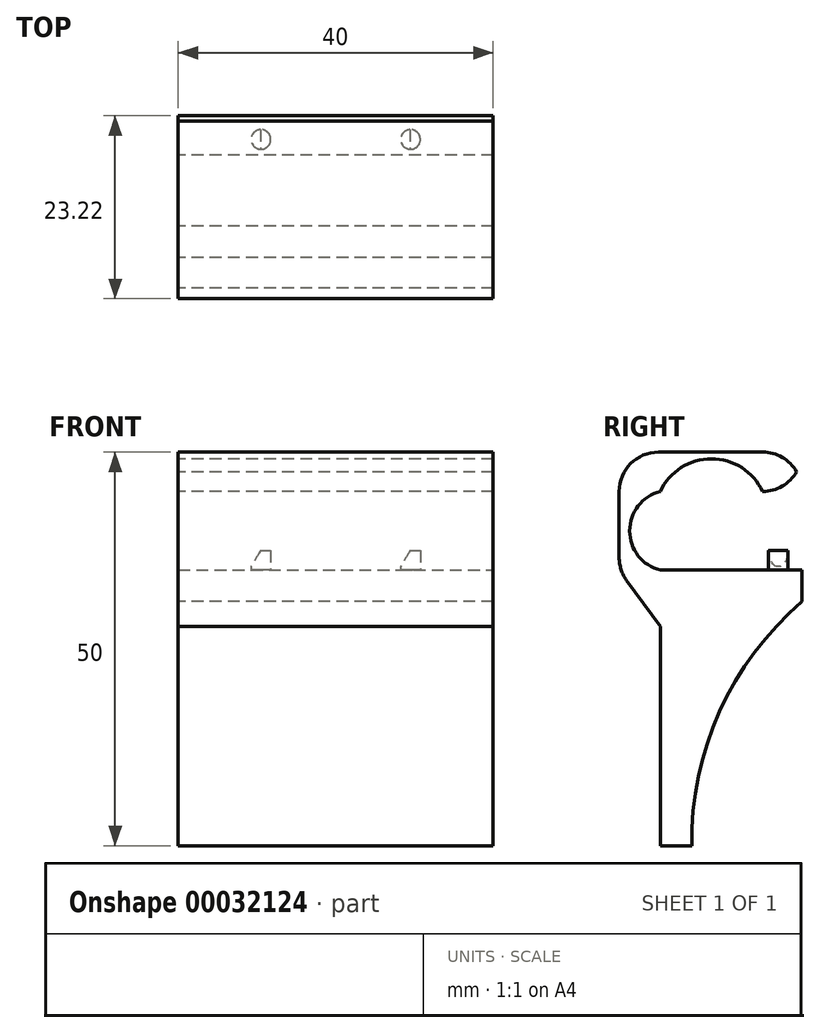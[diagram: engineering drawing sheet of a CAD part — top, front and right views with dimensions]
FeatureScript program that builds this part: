
annotation { "Feature Type Name" : "Feature", "Feature Type Description" : "" }
export const myFeature = defineFeature(function(context is Context, id is Id, definition is map)
    precondition{}
    {
        {
            var Q0;
            Q0=qCreatedBy(makeId("Top.planeOp"),FACE);
            var sketch = newSketch(context, id + "F0", { "sketchPlane" : qUnion([Q0])});
            skLineSegment(sketch, "E0", {"start": v(-9.5, 0) * mm, "end": v(9.5, 0) * mm, "construction": true});
            skCircle(sketch, "E1", {"center": v(-9.5, 0) * mm, "radius": 1.25 * mm});
            skCircle(sketch, "E2.MirrorC", {"center": v(9.5, 0) * mm, "radius": 1.25 * mm});
            skSolve(sketch);
        }
        {
            var Q0;
            Q0=qSketchRegion(id+"F0",true);
            extrude(context, id + "F1", {"entities" : qUnion([Q0]), "depth" : 2.5 * mm});
        }
        {
            var Q0;
            Q0=qCreatedBy(makeId("Top.planeOp"),FACE);
            var sketch = newSketch(context, id + "F2", { "sketchPlane" : qUnion([Q0])});
            skLineSegment(sketch, "E3", {"start": v(0, 0) * mm, "end": v(0, 3) * mm, "construction": true});
            skLineSegment(sketch, "E4", {"start": v(-20, 3) * mm, "end": v(20, 3) * mm});
            skLineSegment(sketch, "E5", {"start": v(-20, 3) * mm, "end": v(-20, -15) * mm});
            skLineSegment(sketch, "E6", {"start": v(20, 3) * mm, "end": v(20, -15) * mm});
            skLineSegment(sketch, "E7", {"start": v(20, -15) * mm, "end": v(-20, -15) * mm});
            skSolve(sketch);
        }
        {
            var Q0;
            Q0=qSketchRegion(id+"F2",true);
            extrude(context, id + "F3", {"entities" : qUnion([Q0]), "operationType" : NewBodyOperationType.ADD, "oppositeDirection" : true, "depth" : 35 * mm});
        }
        {
            var Q0;
            Q0=makeQuery(id+"F3.opExtrude","SWEPT_FACE",FACE,{"disambiguationData":[OSD([sQuery(id+"F2.wireOp",EDGE,"E5")])]});
            var sketch = newSketch(context, id + "F4", { "sketchPlane" : qUnion([Q0])});
            skLineSegment(sketch, "E8", {"start": v(-3, 0) * mm, "end": v(-3, -4) * mm, "construction": true});
            skLineSegment(sketch, "E9", {"start": v(15, -35) * mm, "end": v(11, -35) * mm, "construction": true});
            skArc(sketch, "E10", {"start": v(11, -35) * mm, "mid": v(7.46, -17.94) * mm, "end": v(-3, -4) * mm});
            skLineSegment(sketch, "E11", {"start": v(-3, -4) * mm, "end": v(-3, -35) * mm});
            skLineSegment(sketch, "E12", {"start": v(-3, -35) * mm, "end": v(11, -35) * mm});
            skSolve(sketch);
        }
        {
            var Q0;
            Q0=qSketchRegion(id+"F4",true);
            extrude(context, id + "F5", {"entities" : qUnion([Q0]), "operationType" : NewBodyOperationType.REMOVE, "endBound" : BoundingType.THROUGH_ALL, "oppositeDirection" : true, "depth" : 25 * mm});
        }
        {
            var Q0;
            Q0=makeQuery(id+"F3.opExtrude","SWEPT_FACE",FACE,{"disambiguationData":[OSD([sQuery(id+"F2.wireOp",EDGE,"E5")])]});
            var sketch = newSketch(context, id + "F6", { "sketchPlane" : qUnion([Q0])});
            skLineSegment(sketch, "E13", {"start": v(15, 0) * mm, "end": v(15, 10) * mm, "construction": true});
            skLineSegment(sketch, "E14", {"start": v(15, 10) * mm, "end": v(2, 10) * mm, "construction": true});
            skLineSegment(sketch, "E15", {"start": v(2, 10) * mm, "end": v(-3, 10) * mm});
            skLineSegment(sketch, "E16", {"start": v(-3, 10) * mm, "end": v(-3, 15) * mm});
            skLineSegment(sketch, "E17", {"start": v(-3, 0) * mm, "end": v(-3, 10) * mm, "construction": true});
            skLineSegment(sketch, "E18", {"start": v(15, -7.18) * mm, "end": v(20.22, 0) * mm});
            skLineSegment(sketch, "E19", {"start": v(20.22, 0) * mm, "end": v(20.22, 15) * mm});
            skLineSegment(sketch, "E20", {"start": v(-3, 15) * mm, "end": v(20.22, 15) * mm});
            skLineSegment(sketch, "E21", {"start": v(15, -7.18) * mm, "end": v(15, 0) * mm});
            skArc(sketch, "E22", {"start": v(15, 10) * mm, "mid": v(8.5, 14.13) * mm, "end": v(2, 10) * mm});
            skArc(sketch, "E23", {"start": v(15, 0) * mm, "mid": v(18.88, 5) * mm, "end": v(15, 10) * mm});
            skSolve(sketch);
        }
        {
            var Q0;
            Q0=qSketchRegion(id+"F6",true);
            extrude(context, id + "F7", {"entities" : qUnion([Q0]), "operationType" : NewBodyOperationType.ADD, "oppositeDirection" : true, "depth" : 40 * mm});
        }
        {
            var Q0;
            Q0=makeQuery(id+"F3.opExtrude","SWEPT_FACE",FACE,{"disambiguationData":[OSD([sQuery(id+"F2.wireOp",EDGE,"E4")])]});
            var sketch = newSketch(context, id + "F8", { "sketchPlane" : qUnion([Q0])});
            skLineSegment(sketch, "E24", {"start": v(0, 0) * mm, "end": v(11, 0) * mm, "construction": true});
            skLineSegment(sketch, "E25", {"start": v(11, 0) * mm, "end": v(9.11, 3.27) * mm});
            skLineSegment(sketch, "E26", {"start": v(9.11, 3.27) * mm, "end": v(11, 3.27) * mm});
            skLineSegment(sketch, "E27", {"start": v(11, 3.27) * mm, "end": v(11, 0) * mm});
            skLineSegment(sketch, "E28", {"start": v(0, 0) * mm, "end": v(-8, 0) * mm, "construction": true});
            skLineSegment(sketch, "E29", {"start": v(-8, 0) * mm, "end": v(-9.89, 3.27) * mm});
            skLineSegment(sketch, "E30", {"start": v(-9.89, 3.27) * mm, "end": v(-8, 3.27) * mm});
            skLineSegment(sketch, "E31", {"start": v(-8, 3.27) * mm, "end": v(-8, 0) * mm});
            skSolve(sketch);
        }
        {
            var Q0;
            Q0=qSketchRegion(id+"F8",true);
            extrude(context, id + "F9", {"entities" : qUnion([Q0]), "operationType" : NewBodyOperationType.REMOVE, "oppositeDirection" : true, "depth" : 10 * mm});
        }
        {
            var Q0;
            Q0=makeQuery(id+"F7.opExtrude","SWEPT_EDGE",EDGE,{"disambiguationData":[OSD([sQuery(id+"F6.wireOp",EDGE,"E19"),sQuery(id+"F6.wireOp",EDGE,"E20")])]});
            var Q1;
            Q1=makeQuery(id+"F7.opExtrude","SWEPT_EDGE",EDGE,{"disambiguationData":[OSD([sQuery(id+"F6.wireOp",EDGE,"E16"),sQuery(id+"F6.wireOp",EDGE,"E20")])]});
            var Q2;
            Q2=makeQuery(id+"F7.opExtrude","SWEPT_EDGE",EDGE,{"disambiguationData":[OSD([sQuery(id+"F6.wireOp",EDGE,"E18"),sQuery(id+"F6.wireOp",EDGE,"E19")])]});
            var Q3;
            Q3=makeQuery(id+"F7.opExtrude","SWEPT_EDGE",EDGE,{"disambiguationData":[OSD([sQuery(id+"F2.wireOp",EDGE,"E5"),sQuery(id+"F2.wireOp",EDGE,"E7"),sQuery(id+"F6.wireOp",EDGE,"E18"),sQuery(id+"F6.wireOp",EDGE,"E21")])]});
            var Q4;
            Q4=makeQuery(id+"F7.opExtrude","SWEPT_EDGE",EDGE,{"disambiguationData":[OSD([sQuery(id+"F6.wireOp",EDGE,"E15"),sQuery(id+"F6.wireOp",EDGE,"E16")])]});
            fillet(context, id + "F10", {"entities" : qUnion([Q0, Q1, Q2, Q3, Q4]), "radius" : 5 * mm, "tangentPropagation" : true, "allowEdgeOverflow" : false});
        }
    });
